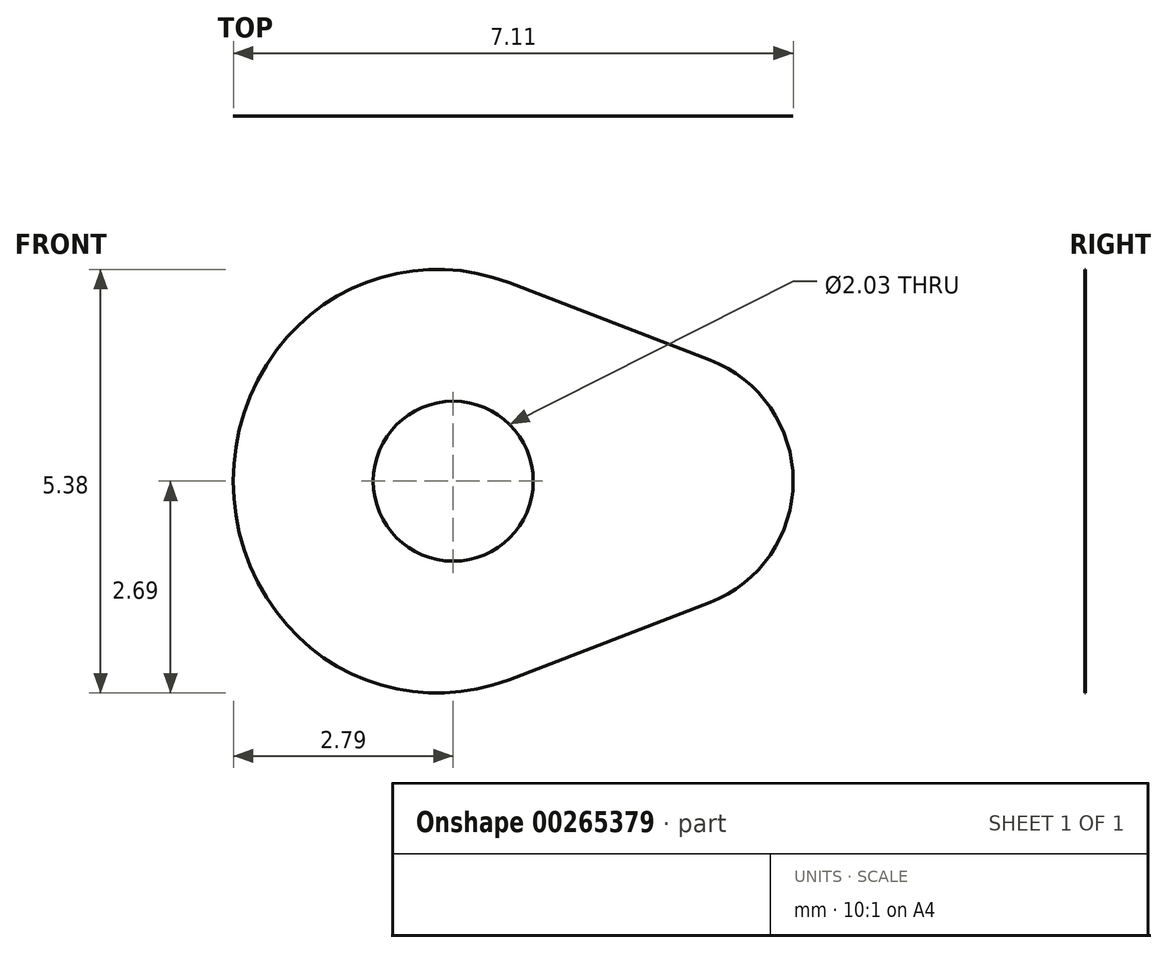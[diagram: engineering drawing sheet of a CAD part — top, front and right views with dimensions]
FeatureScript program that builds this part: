
annotation { "Feature Type Name" : "Feature", "Feature Type Description" : "" }
export const myFeature = defineFeature(function(context is Context, id is Id, definition is map)
    precondition{}
    {
        {
            var Q0;
            Q0=qCreatedBy(makeId("Front.planeOp"),FACE);
            var sketch = newSketch(context, id + "F0", { "sketchPlane" : qUnion([Q0])});
            skArc(sketch, "E0", {"start": v(0, 2.8) * mm, "mid": v(-2.8, 0) * mm, "end": v(0, -2.8) * mm});
            skArc(sketch, "E1", {"start": v(3.26, -1.54) * mm, "mid": v(4.32, 0) * mm, "end": v(3.26, 1.54) * mm});
            skCircle(sketch, "E2", {"center": v(0, 0) * mm, "radius": 1.02 * mm});
            skLineSegment(sketch, "E3", {"start": v(0, 2.8) * mm, "end": v(3.26, 1.54) * mm});
            skLineSegment(sketch, "E4", {"start": v(0, -2.8) * mm, "end": v(3.26, -1.54) * mm});
            skSolve(sketch);
        }
        {
            var Q0;
            Q0 = qSketchRegion(id + "F0", true);
            extrude(context, id + "F1", {"entities" : qUnion([Q0]), "depth" : .175 / 50.8 * mm});
        }
        {
            var Q0;
            Q0=makeQuery(id+"F1.opExtrude","SWEPT_EDGE",EDGE,{"disambiguationData":[OSD([sQuery(id+"F0.wireOp",EDGE,"E0"),sQuery(id+"F0.wireOp",EDGE,"E3")])]});
            fillet(context, id + "F2", {"entities" : qUnion([Q0]), "radius" : 2.54 * mm, "tangentPropagation" : true, "allowEdgeOverflow" : false});
        }
        {
            var Q0;
            Q0=makeQuery(id+"F1.opExtrude","SWEPT_EDGE",EDGE,{"disambiguationData":[OSD([sQuery(id+"F0.wireOp",EDGE,"E0"),sQuery(id+"F0.wireOp",EDGE,"E4")])]});
            fillet(context, id + "F3", {"entities" : qUnion([Q0]), "radius" : 2.54 * mm, "tangentPropagation" : true, "allowEdgeOverflow" : false});
        }
    });
